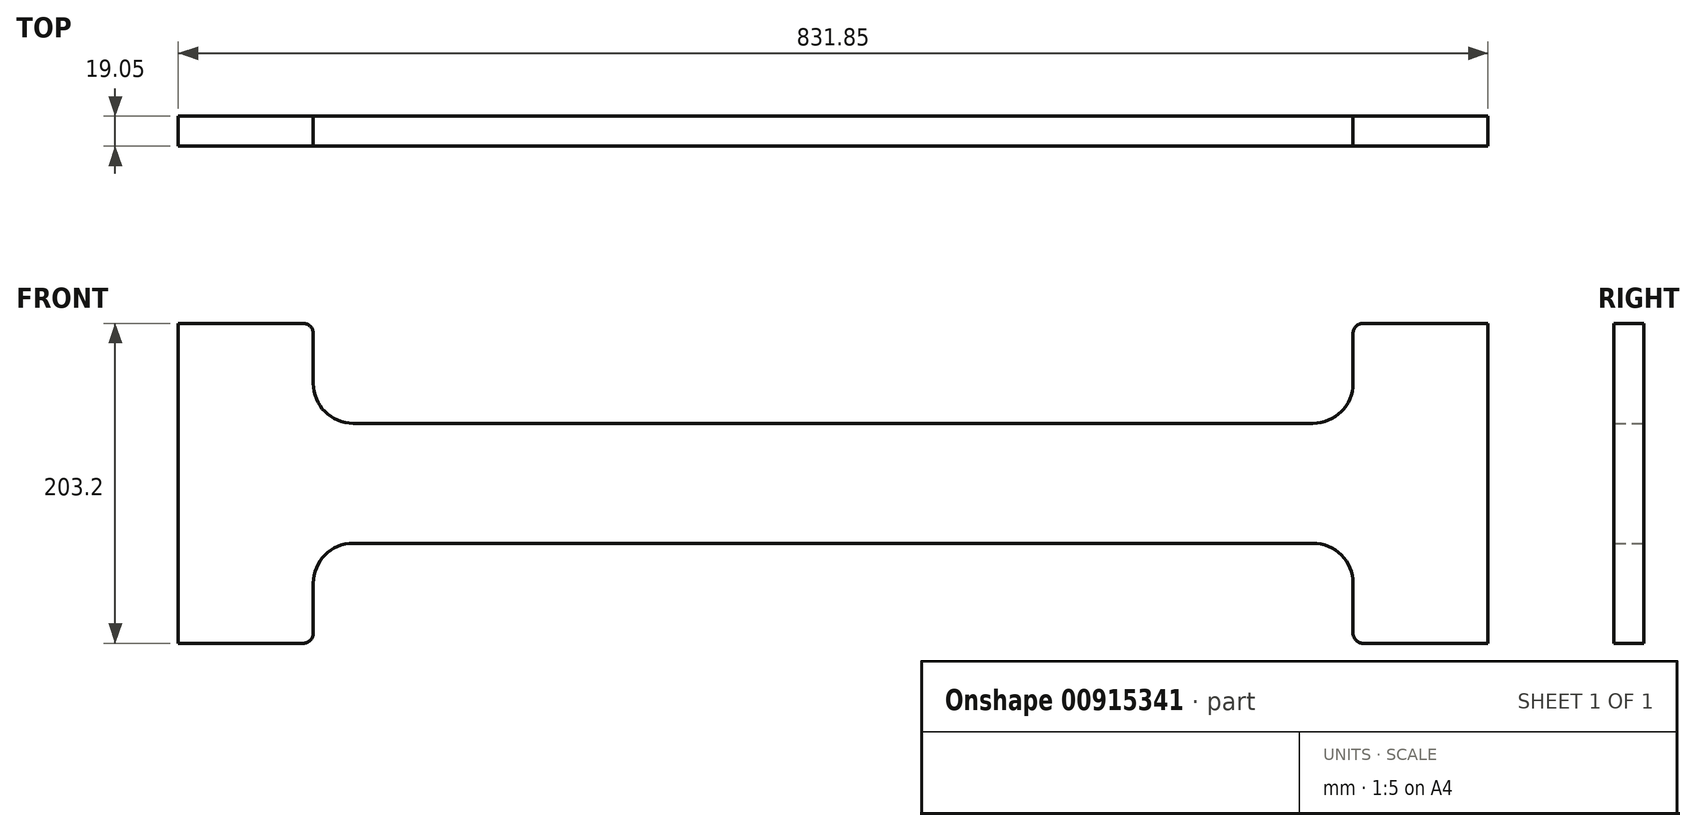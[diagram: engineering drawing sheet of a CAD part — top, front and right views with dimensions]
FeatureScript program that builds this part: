
annotation { "Feature Type Name" : "Feature", "Feature Type Description" : "" }
export const myFeature = defineFeature(function(context is Context, id is Id, definition is map)
    precondition{}
    {
        {
            var Q0;
            Q0=qCreatedBy(makeId("Front.planeOp"),FACE);
            var sketch = newSketch(context, id + "F0", { "sketchPlane" : qUnion([Q0])});
            skLineSegment(sketch, "E0.bottom", {"start": v(-831.85, 203.2) * mm, "end": v(-752.48, 203.2) * mm});
            skLineSegment(sketch, "E0.top", {"start": v(-831.85, 0) * mm, "end": v(-752.48, 0) * mm});
            skLineSegment(sketch, "E0.left", {"start": v(-831.85, 203.2) * mm, "end": v(-831.85, 0) * mm});
            skLineSegment(sketch, "E0.right", {"start": v(0, 203.2) * mm, "end": v(0, 0) * mm});
            skLineSegment(sketch, "E1", {"start": v(-831.85, 101.6) * mm, "end": v(0, 101.6) * mm, "construction": true});
            skLineSegment(sketch, "E2", {"start": v(-415.93, 0) * mm, "end": v(-415.93, 203.2) * mm, "construction": true});
            skLineSegment(sketch, "E3.top", {"start": v(-720.73, 139.7) * mm, "end": v(-111.13, 139.7) * mm});
            skLineSegment(sketch, "E3.left", {"start": v(-746.13, 196.85) * mm, "end": v(-746.13, 165.1) * mm});
            skLineSegment(sketch, "E3.right", {"start": v(-85.73, 196.85) * mm, "end": v(-85.73, 165.1) * mm});
            skPoint(sketch, "E4.visualSharp", {"position": v(-746.13, 139.7) * mm});
            skArc(sketch, "E4.filletArc", {"start": v(-746.13, 165.1) * mm, "mid": v(-738.69, 147.14) * mm, "end": v(-720.73, 139.7) * mm});
            skPoint(sketch, "E5.visualSharp", {"position": v(-85.73, 139.7) * mm});
            skArc(sketch, "E5.filletArc", {"start": v(-111.13, 139.7) * mm, "mid": v(-93.16, 147.14) * mm, "end": v(-85.73, 165.1) * mm});
            skLineSegment(sketch, "E6.MirrorCS", {"start": v(-85.73, 6.35) * mm, "end": v(-85.73, 38.1) * mm});
            skPoint(sketch, "E7.MirrorP", {"position": v(-85.73, 63.5) * mm});
            skArc(sketch, "E8.MirrorCS", {"start": v(-111.13, 63.5) * mm, "mid": v(-93.16, 56.06) * mm, "end": v(-85.73, 38.1) * mm});
            skLineSegment(sketch, "E9.MirrorCS", {"start": v(-720.73, 63.5) * mm, "end": v(-111.13, 63.5) * mm});
            skArc(sketch, "E10.MirrorCS", {"start": v(-746.13, 38.1) * mm, "mid": v(-738.69, 56.06) * mm, "end": v(-720.73, 63.5) * mm});
            skLineSegment(sketch, "E11.MirrorCS", {"start": v(-746.13, 6.35) * mm, "end": v(-746.13, 38.1) * mm});
            skLineSegment(sketch, "E12.trimOffspring", {"start": v(-79.38, 203.2) * mm, "end": v(0, 203.2) * mm});
            skLineSegment(sketch, "E13.trimOffspring", {"start": v(-79.38, 0) * mm, "end": v(0, 0) * mm});
            skPoint(sketch, "E14.visualSharp", {"position": v(-746.13, 0) * mm});
            skArc(sketch, "E14.filletArc", {"start": v(-752.48, 0) * mm, "mid": v(-747.98, 1.86) * mm, "end": v(-746.13, 6.35) * mm});
            skPoint(sketch, "E15.visualSharp", {"position": v(-85.73, 0) * mm});
            skArc(sketch, "E15.filletArc", {"start": v(-85.72, 6.35) * mm, "mid": v(-83.87, 1.86) * mm, "end": v(-79.38, 0) * mm});
            skPoint(sketch, "E16.visualSharp", {"position": v(-85.73, 203.2) * mm});
            skArc(sketch, "E16.filletArc", {"start": v(-79.38, 203.2) * mm, "mid": v(-83.87, 201.34) * mm, "end": v(-85.73, 196.85) * mm});
            skPoint(sketch, "E17.visualSharp", {"position": v(-746.13, 203.2) * mm});
            skArc(sketch, "E17.filletArc", {"start": v(-746.13, 196.85) * mm, "mid": v(-747.98, 201.34) * mm, "end": v(-752.48, 203.2) * mm});
            skSolve(sketch);
        }
        {
            var Q0;
            Q0=makeQuery(id+"F0.imprint","IMPRINT",FACE,{"disambiguationData":[TD([[makeQuery(id+"F0.imprint","IMPRINT",EDGE,{"derivedFrom":sQuery(id+"F0.wireOp",EDGE,"E0.bottom")}),-1.0]])]});
            extrude(context, id + "F1", {"entities" : qUnion([Q0]), "depth" : 19.05 * mm, "offsetDistance" : 25.4 * mm});
        }
    });
